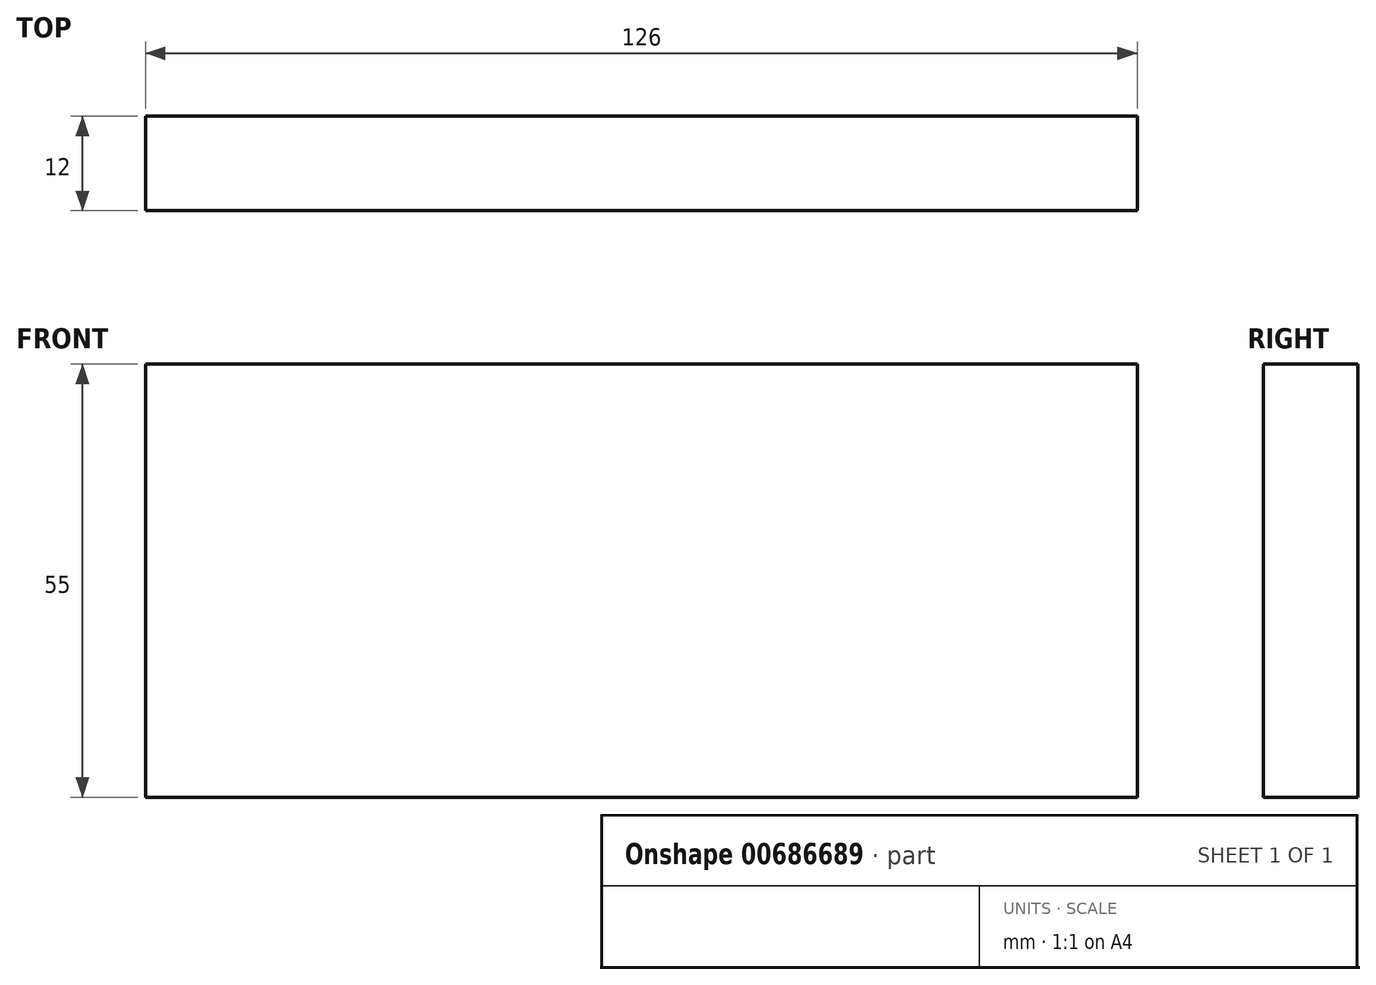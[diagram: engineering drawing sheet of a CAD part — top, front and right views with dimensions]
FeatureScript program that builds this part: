
annotation { "Feature Type Name" : "Feature", "Feature Type Description" : "" }
export const myFeature = defineFeature(function(context is Context, id is Id, definition is map)
    precondition{}
    {
        {
            var Q0;
            Q0=qCreatedBy(makeId("Front.planeOp"),FACE);
            var sketch = newSketch(context, id + "F0", { "sketchPlane" : qUnion([Q0])});
            skLineSegment(sketch, "E0.bottom", {"start": v(0, 0) * mm, "end": v(126, 0) * mm});
            skLineSegment(sketch, "E0.top", {"start": v(0, 55) * mm, "end": v(126, 55) * mm});
            skLineSegment(sketch, "E0.left", {"start": v(0, 0) * mm, "end": v(0, 55) * mm});
            skLineSegment(sketch, "E0.right", {"start": v(126, 0) * mm, "end": v(126, 55) * mm});
            skSolve(sketch);
        }
        {
            var Q0;
            Q0=qSketchRegion(id+"F0",true);
            extrude(context, id + "F1", {"entities" : qUnion([Q0]), "depth" : 12 * mm, "offsetDistance" : 25 * mm});
        }
    });
